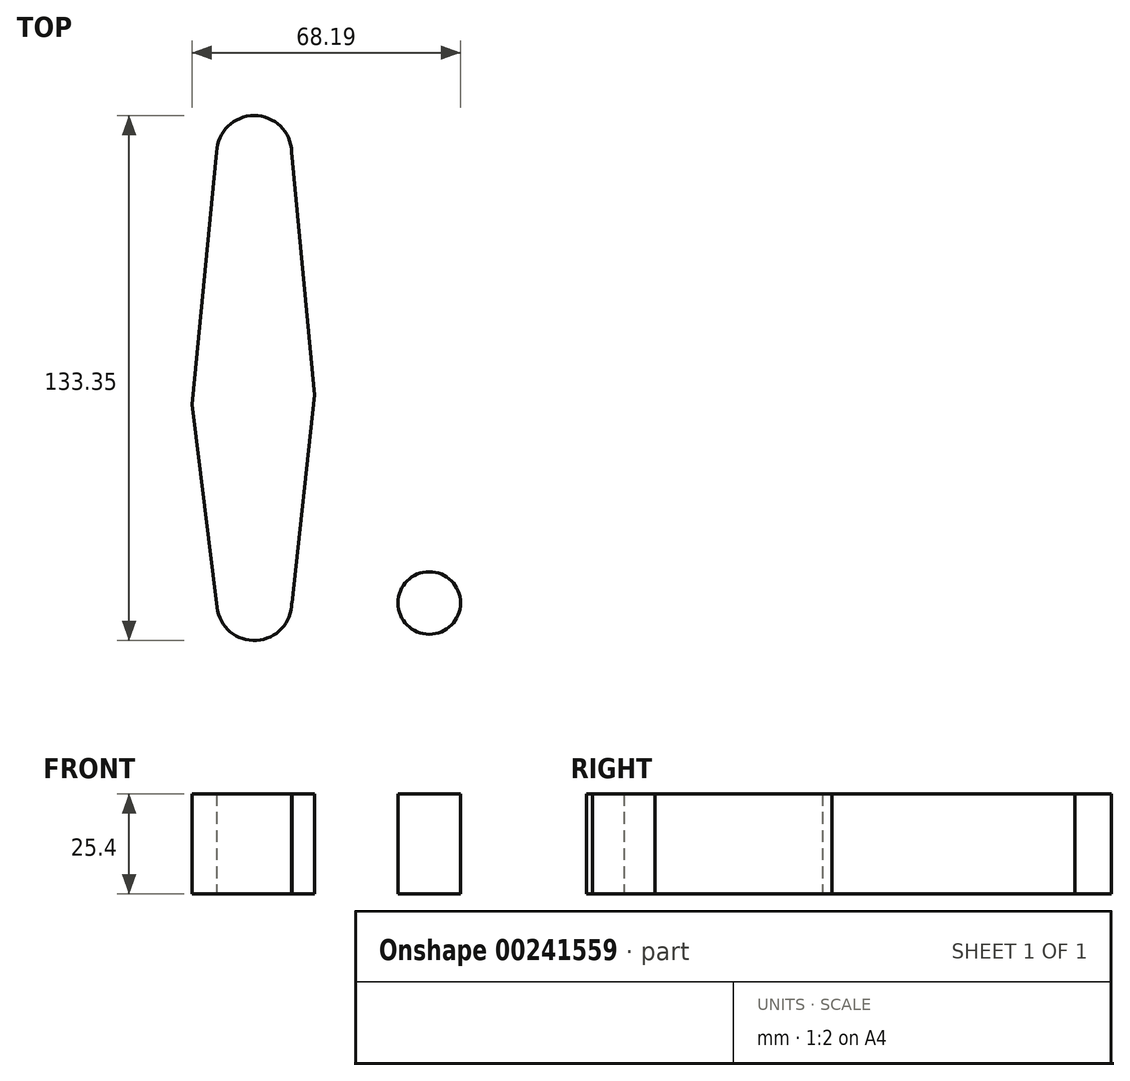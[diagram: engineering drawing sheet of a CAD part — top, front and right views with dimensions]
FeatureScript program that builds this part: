
annotation { "Feature Type Name" : "Feature", "Feature Type Description" : "" }
export const myFeature = defineFeature(function(context is Context, id is Id, definition is map)
    precondition{}
    {
        {
            var Q0;
            Q0=qCreatedBy(makeId("Top.planeOp"),FACE);
            var sketch = newSketch(context, id + "F0", { "sketchPlane" : qUnion([Q0])});
            skLineSegment(sketch, "E0", {"start": v(0, 81.26) * mm, "end": v(0, -33.04) * mm});
            skLineSegment(sketch, "E1", {"start": v(0, -33.04) * mm, "end": v(44.45, -33.04) * mm});
            skCircle(sketch, "E2", {"center": v(0, 81.26) * mm, "radius": 9.53 * mm});
            skCircle(sketch, "E3", {"center": v(0, 15.8) * mm, "radius": 15.88 * mm});
            skCircle(sketch, "E4", {"center": v(0, -33.04) * mm, "radius": 9.53 * mm});
            skCircle(sketch, "E5", {"center": v(44.45, -33.04) * mm, "radius": 7.94 * mm});
            skLineSegment(sketch, "E6", {"start": v(-9.52, 81.53) * mm, "end": v(-15.8, 17.36) * mm});
            skLineSegment(sketch, "E7", {"start": v(9.52, 81.57) * mm, "end": v(15.37, 19.8) * mm});
            skLineSegment(sketch, "E8", {"start": v(-15.8, 17.36) * mm, "end": v(-9.45, -34.2) * mm});
            skLineSegment(sketch, "E9", {"start": v(15.37, 19.8) * mm, "end": v(9.58, -33.04) * mm});
            skLineSegment(sketch, "E10", {"start": v(9.58, -33.04) * mm, "end": v(15.37, -30.2) * mm});
            skSolve(sketch);
        }
        {
            var Q0;
            {var subQ5=sQuery(id+"F0.wireOp",EDGE,"E7");Q0=makeQuery(id+"F0.imprint","IMPRINT",FACE,{"disambiguationData":[TD([[makeQuery(id+"F0.imprint","IMPRINT",EDGE,{"derivedFrom":subQ5}),-1.0]])]});}
            var Q1;
            {var subQ5=sQuery(id+"F0.wireOp",EDGE,"E6");Q1=makeQuery(id+"F0.imprint","IMPRINT",FACE,{"disambiguationData":[TD([[makeQuery(id+"F0.imprint","IMPRINT",EDGE,{"derivedFrom":subQ5}),1.0]])]});}
            var Q2;
            {var subQ0=sQuery(id+"F0.wireOp",EDGE,"E3");var subQ1=sQuery(id+"F0.wireOp",EDGE,"E0");var subQ2=makeQuery(id+"F0.imprint","INTERSECT",VERTEX,{"disambiguationData":[OD(1.0)],"derivedFrom":[subQ1,subQ0]});Q2=makeQuery(id+"F0.imprint","IMPRINT",FACE,{"disambiguationData":[TD([[makeQuery(id+"F0.imprint","IMPRINT",EDGE,{"disambiguationData":[TD([[subQ2,-1.0]])],"derivedFrom":subQ1}),-1.0]])]});}
            var Q3;
            {var subQ3=sQuery(id+"F0.wireOp",EDGE,"E0");var subQ6=sQuery(id+"F0.wireOp",EDGE,"E3");var subQ8=makeQuery(id+"F0.imprint","INTERSECT",VERTEX,{"disambiguationData":[OD(1.0)],"derivedFrom":[subQ3,subQ6]});Q3=makeQuery(id+"F0.imprint","IMPRINT",FACE,{"disambiguationData":[TD([[makeQuery(id+"F0.imprint","IMPRINT",EDGE,{"disambiguationData":[TD([[subQ8,-1.0]])],"derivedFrom":subQ3}),1.0]])]});}
            var Q4;
            Q4=makeQuery(id+"F0.imprint","IMPRINT",FACE,{"disambiguationData":[TD([[makeQuery(id+"F0.imprint","IMPRINT",EDGE,{"derivedFrom":sQuery(id+"F0.wireOp",EDGE,"E5")}),1.0]])]});
            var Q5;
            {var subQ0=sQuery(id+"F0.wireOp",EDGE,"E1");var subQ1=sQuery(id+"F0.wireOp",EDGE,"E0");var subQ2=makeQuery(id+"F0.imprint","INTERSECT",VERTEX,{"derivedFrom":[subQ1,subQ0]});Q5=makeQuery(id+"F0.imprint","IMPRINT",FACE,{"disambiguationData":[TD([[makeQuery(id+"F0.imprint","IMPRINT",EDGE,{"disambiguationData":[TD([[subQ2,1.0]])],"derivedFrom":subQ1}),-1.0]])]});}
            var Q6;
            {var subQ0=sQuery(id+"F0.wireOp",EDGE,"E1");var subQ1=sQuery(id+"F0.wireOp",EDGE,"E0");var subQ2=makeQuery(id+"F0.imprint","INTERSECT",VERTEX,{"derivedFrom":[subQ1,subQ0]});Q6=makeQuery(id+"F0.imprint","IMPRINT",FACE,{"disambiguationData":[TD([[makeQuery(id+"F0.imprint","IMPRINT",EDGE,{"disambiguationData":[TD([[subQ2,1.0]])],"derivedFrom":subQ1}),1.0]])]});}
            var Q7;
            {var subQ0=sQuery(id+"F0.wireOp",EDGE,"E2");var subQ1=makeQuery(id+"F0.imprint","INTERSECT",VERTEX,{"derivedFrom":[subQ0,sQuery(id+"F0.wireOp",EDGE,"E6")]});Q7=makeQuery(id+"F0.imprint","IMPRINT",FACE,{"disambiguationData":[TD([[makeQuery(id+"F0.imprint","IMPRINT",EDGE,{"disambiguationData":[TD([[subQ1,1.0]])],"derivedFrom":subQ0}),1.0]])]});}
            var Q8;
            {var subQ0=sQuery(id+"F0.wireOp",EDGE,"E3");var subQ1=sQuery(id+"F0.wireOp",EDGE,"E0");var subQ2=makeQuery(id+"F0.imprint","INTERSECT",VERTEX,{"disambiguationData":[OD(0.0)],"derivedFrom":[subQ1,subQ0]});Q8=makeQuery(id+"F0.imprint","IMPRINT",FACE,{"disambiguationData":[TD([[makeQuery(id+"F0.imprint","IMPRINT",EDGE,{"disambiguationData":[TD([[subQ2,-1.0]])],"derivedFrom":subQ1}),1.0]])]});}
            var Q9;
            {var subQ0=sQuery(id+"F0.wireOp",EDGE,"E3");var subQ1=sQuery(id+"F0.wireOp",EDGE,"E0");var subQ2=makeQuery(id+"F0.imprint","INTERSECT",VERTEX,{"disambiguationData":[OD(0.0)],"derivedFrom":[subQ1,subQ0]});Q9=makeQuery(id+"F0.imprint","IMPRINT",FACE,{"disambiguationData":[TD([[makeQuery(id+"F0.imprint","IMPRINT",EDGE,{"disambiguationData":[TD([[subQ2,-1.0]])],"derivedFrom":subQ1}),-1.0]])]});}
            extrude(context, id + "F1", {"entities" : qUnion([Q0, Q1, Q2, Q3, Q4, Q5, Q6, Q7, Q8, Q9]), "depth" : 25.4 * mm});
        }
    });
